# Revit family: rba-bim-rba5502 Series
name_source: partatom
category: Plumbing Fixtures
revit_build: Autodesk Revit 2018 (Build: 20170223_1515(x64)
units: mm (PartAtom-declared; Revit-internal decimal feet)

## family parameters
Always vertical = Yes
Cut with Voids When Loaded = No
Part Type = Normal
Room Calculation Point = No
Round Connector Dimension = Use Diameter
Shared = Yes
Work Plane-Based = No

## types (7) — shared parameters
CW Connection = Yes
HW Connection = Yes
Logo Distance = 50 mm  [stored 0.164042 ft]
Manufacturer = RBA Group
Middle Bracket = Yes
Vent Connection = Yes
Waste Connection = Yes
zero-valued in all types: No. of Outlets

## per-type parameters (varying)
| type | 120 | 160 | 200 | 240 | Depth | Description | L1 | L2 | L3 | L4 | L5 | Length | Materials and Finishes | Model | Modified Issue |
| RBA5502-120 | Yes | No | No | No | 140 mm | 1200mm Wash Trough | 280 mm | 280 mm | 280 mm | 280 mm | 0 mm  [stored 0 ft] | 1200 mm | <By Category> | RBA5502-120 | 20210728.01 |
| RBA5502-150 | No | No | No | Yes | 131 mm | 1500mm Wash Trough | 380 mm | 380 mm | 380 mm | 380 mm | 40 mm | 1500 mm | Stainless Steel AISI 304 Satin Finish, 1.2mm | RBA5502-150 | 20210504.01 |
| RBA5502-180 | No | No | No | Yes | 131 mm | 1800mm Wash Trough | 380 mm | 380 mm | 380 mm | 380 mm | 40 mm | 1800 mm | Stainless Steel AISI 304 Satin Finish, 1.2mm | RBA5502-180 | 20210504.01 |
| RBA5502-240 | No | No | No | Yes | 131 mm | 2400mm Wash Trough | 280 mm | 280 mm | 280 mm | 280 mm | 0 mm  [stored 0 ft] | 2400 mm | <By Category> | RBA5502-240 | 20210504.01 |
| RBA5502-300 | No | No | No | Yes | 131 mm | 3000mm Wash Trough | 380 mm | 380 mm | 380 mm | 380 mm | 40 mm | 3000 mm | Stainless Steel AISI 304 Satin Finish, 1.2mm | RBA5502-300 | 20210504.01 |
| RBA5502-160 | No | Yes | No | No | 138 mm | 1600mm Wash Trough | 260 mm | 260 mm | 260 mm | 260 mm | 0 mm  [stored 0 ft] | 1600 mm | Stainless Steel AISI 304 Satin Finish, 1.2mm | RBA5502-160 | 20210504.01 |
| RBA5502-200 | No | No | Yes | No | 134 mm | 2000mm Wash Trough | 260 mm | 260 mm | 260 mm | 260 mm | 130 mm  [stored 0.426509 ft] | 2000 mm | Stainless Steel AISI 304 Satin Finish, 1.2mm | RBA5502-180 | 20210504.01 |

note: [stored X ft] marks values corroborated as IEEE doubles in the binary element streams (Revit-internal decimal feet)

## geometry (parser evidence)
native form markers: Blend x2, Sweep x1
no freeform markers — native parametric forms only
